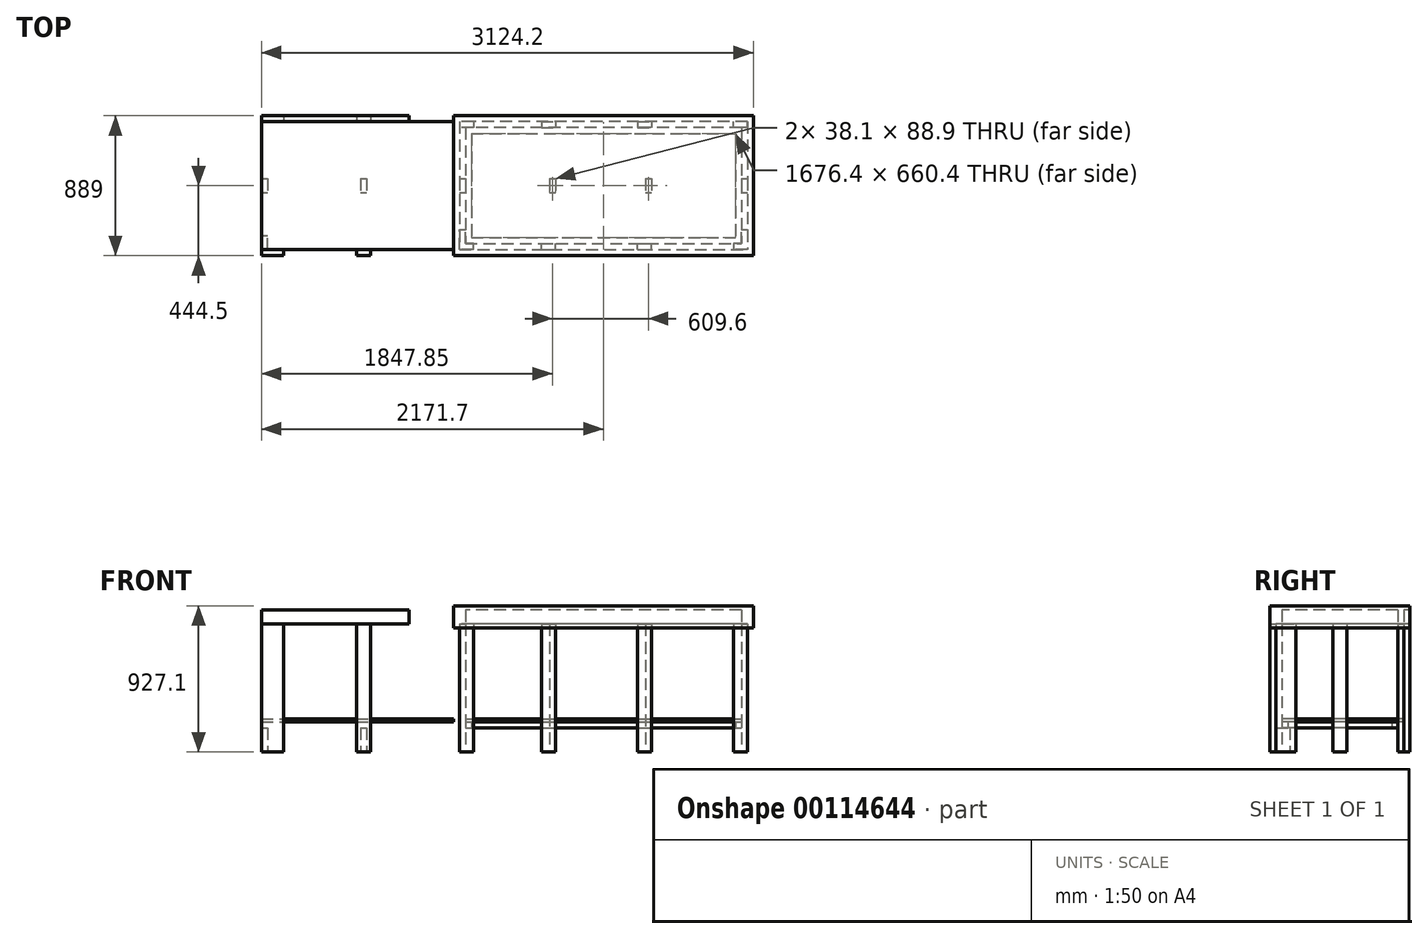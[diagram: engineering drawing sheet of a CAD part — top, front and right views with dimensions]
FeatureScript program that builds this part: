
annotation { "Feature Type Name" : "Feature", "Feature Type Description" : "" }
export const myFeature = defineFeature(function(context is Context, id is Id, definition is map)
    precondition{}
    {
        {
            var Q0;
            Q0=qCreatedBy(makeId("Top.planeOp"),FACE);
            cPlane(context, id + "F0", {"entities" : qUnion([Q0]), "cplaneType" : CPlaneType.OFFSET, "offset" : 152.4 * mm, "width" : 152.4 * mm, "height" : 152.4 * mm});
        }
        {
            var Q0;
            Q0=qCreatedBy(makeId("Top.planeOp"),FACE);
            var sketch = newSketch(context, id + "F1", { "sketchPlane" : qUnion([Q0])});
            skLineSegment(sketch, "E0.bottom", {"start": v(0, 0) * mm, "end": v(3124.2, 0) * mm});
            skLineSegment(sketch, "E0.top", {"start": v(0, 889) * mm, "end": v(3124.2, 889) * mm});
            skLineSegment(sketch, "E0.left", {"start": v(0, 0) * mm, "end": v(0, 889) * mm});
            skLineSegment(sketch, "E0.right", {"start": v(3124.2, 0) * mm, "end": v(3124.2, 889) * mm});
            skLineSegment(sketch, "E1.bottom", {"start": v(0, 889) * mm, "end": v(1295.4, 889) * mm});
            skLineSegment(sketch, "E1.top", {"start": v(0, 2184.4) * mm, "end": v(1295.4, 2184.4) * mm});
            skLineSegment(sketch, "E1.left", {"start": v(0, 889) * mm, "end": v(0, 2184.4) * mm});
            skLineSegment(sketch, "E1.right", {"start": v(1295.4, 889) * mm, "end": v(1295.4, 2184.4) * mm});
            skLineSegment(sketch, "E2.bottom", {"start": v(0, 0) * mm, "end": v(1295.4, 0) * mm});
            skLineSegment(sketch, "E2.top", {"start": v(0, -1295.4) * mm, "end": v(1295.4, -1295.4) * mm});
            skLineSegment(sketch, "E2.left", {"start": v(0, 0) * mm, "end": v(0, -1295.4) * mm});
            skLineSegment(sketch, "E2.right", {"start": v(1295.4, 0) * mm, "end": v(1295.4, -1295.4) * mm});
            skLineSegment(sketch, "E3.0", {"start": v(38.1, 927.1) * mm, "end": v(38.1, 2146.3) * mm});
            skLineSegment(sketch, "E3.1", {"start": v(38.1, 927.1) * mm, "end": v(1257.3, 927.1) * mm});
            skLineSegment(sketch, "E3.2", {"start": v(1257.3, 927.1) * mm, "end": v(1257.3, 2146.3) * mm});
            skLineSegment(sketch, "E3.3", {"start": v(38.1, 2146.3) * mm, "end": v(1257.3, 2146.3) * mm});
            skLineSegment(sketch, "E4.0", {"start": v(1257.3, -38.1) * mm, "end": v(1257.3, -1257.3) * mm});
            skLineSegment(sketch, "E4.1", {"start": v(38.1, -38.1) * mm, "end": v(1257.3, -38.1) * mm});
            skLineSegment(sketch, "E4.2", {"start": v(38.1, -38.1) * mm, "end": v(38.1, -1257.3) * mm});
            skLineSegment(sketch, "E4.3", {"start": v(38.1, -1257.3) * mm, "end": v(1257.3, -1257.3) * mm});
            skLineSegment(sketch, "E5.0", {"start": v(38.1, 38.1) * mm, "end": v(38.1, 850.9) * mm});
            skLineSegment(sketch, "E5.1", {"start": v(38.1, 38.1) * mm, "end": v(3086.1, 38.1) * mm});
            skLineSegment(sketch, "E5.2", {"start": v(3086.1, 38.1) * mm, "end": v(3086.1, 850.9) * mm});
            skLineSegment(sketch, "E5.3", {"start": v(38.1, 850.9) * mm, "end": v(3086.1, 850.9) * mm});
            skLineSegment(sketch, "E6", {"start": v(647.7, 2146.3) * mm, "end": v(647.7, 927.1) * mm, "construction": true});
            skLineSegment(sketch, "E7", {"start": v(38.1, 1536.7) * mm, "end": v(1257.3, 1536.7) * mm, "construction": true});
            skLineSegment(sketch, "E8", {"start": v(647.7, -38.1) * mm, "end": v(647.7, -1257.3) * mm, "construction": true});
            skLineSegment(sketch, "E9", {"start": v(38.1, -647.7) * mm, "end": v(1257.3, -647.7) * mm, "construction": true});
            skLineSegment(sketch, "E10", {"start": v(38.1, 444.5) * mm, "end": v(3086.1, 444.5) * mm, "construction": true});
            skSolve(sketch);
        }
        {
            var Q0;
            Q0=qCreatedBy(makeId("Top.planeOp"),FACE);
            var sketch = newSketch(context, id + "F2", { "sketchPlane" : qUnion([Q0])});
            skLineSegment(sketch, "E11.bottom", {"start": v(3086.1, 812.8) * mm, "end": v(2997.2, 812.8) * mm});
            skLineSegment(sketch, "E11.top", {"start": v(3086.1, 850.9) * mm, "end": v(2997.2, 850.9) * mm});
            skLineSegment(sketch, "E11.left", {"start": v(3086.1, 812.8) * mm, "end": v(3086.1, 850.9) * mm});
            skLineSegment(sketch, "E11.right", {"start": v(2997.2, 812.8) * mm, "end": v(2997.2, 850.9) * mm});
            skLineSegment(sketch, "E12.bottom", {"start": v(3048, 812.8) * mm, "end": v(3086.1, 812.8) * mm});
            skLineSegment(sketch, "E12.top", {"start": v(3048, 723.9) * mm, "end": v(3086.1, 723.9) * mm});
            skLineSegment(sketch, "E12.left", {"start": v(3048, 812.8) * mm, "end": v(3048, 723.9) * mm});
            skLineSegment(sketch, "E12.right", {"start": v(3086.1, 812.8) * mm, "end": v(3086.1, 723.9) * mm});
            skLineSegment(sketch, "E13.bottom", {"start": v(2387.6, 850.9) * mm, "end": v(2476.5, 850.9) * mm});
            skLineSegment(sketch, "E13.top", {"start": v(2387.6, 812.8) * mm, "end": v(2476.5, 812.8) * mm});
            skLineSegment(sketch, "E13.left", {"start": v(2387.6, 850.9) * mm, "end": v(2387.6, 812.8) * mm});
            skLineSegment(sketch, "E13.right", {"start": v(2476.5, 850.9) * mm, "end": v(2476.5, 812.8) * mm});
            skLineSegment(sketch, "E14.bottom", {"start": v(1778, 850.9) * mm, "end": v(1866.9, 850.9) * mm});
            skLineSegment(sketch, "E14.top", {"start": v(1778, 812.8) * mm, "end": v(1866.9, 812.8) * mm});
            skLineSegment(sketch, "E14.left", {"start": v(1778, 850.9) * mm, "end": v(1778, 812.8) * mm});
            skLineSegment(sketch, "E14.right", {"start": v(1866.9, 850.9) * mm, "end": v(1866.9, 812.8) * mm});
            skLineSegment(sketch, "E15.bottom", {"start": v(1346.2, 850.9) * mm, "end": v(1257.3, 850.9) * mm});
            skLineSegment(sketch, "E15.top", {"start": v(1346.2, 812.8) * mm, "end": v(1257.3, 812.8) * mm});
            skLineSegment(sketch, "E15.left", {"start": v(1346.2, 850.9) * mm, "end": v(1346.2, 812.8) * mm});
            skLineSegment(sketch, "E15.right", {"start": v(1257.3, 850.9) * mm, "end": v(1257.3, 812.8) * mm});
            skLineSegment(sketch, "E16.bottom", {"start": v(1257.3, 812.8) * mm, "end": v(1295.4, 812.8) * mm});
            skLineSegment(sketch, "E16.top", {"start": v(1257.3, 723.9) * mm, "end": v(1295.4, 723.9) * mm});
            skLineSegment(sketch, "E16.left", {"start": v(1257.3, 812.8) * mm, "end": v(1257.3, 723.9) * mm});
            skLineSegment(sketch, "E16.right", {"start": v(1295.4, 812.8) * mm, "end": v(1295.4, 723.9) * mm});
            skPoint(sketch, "E17", {"position": v(1301.75, 812.8) * mm});
            skLineSegment(sketch, "E18.bottom", {"start": v(0, 889) * mm, "end": v(139.7, 889) * mm});
            skLineSegment(sketch, "E18.top", {"start": v(0, 850.9) * mm, "end": v(139.7, 850.9) * mm});
            skLineSegment(sketch, "E18.left", {"start": v(0, 889) * mm, "end": v(0, 850.9) * mm});
            skLineSegment(sketch, "E18.right", {"start": v(139.7, 889) * mm, "end": v(139.7, 850.9) * mm});
            skLineSegment(sketch, "E19.bottom", {"start": v(0, 850.9) * mm, "end": v(38.1, 850.9) * mm});
            skLineSegment(sketch, "E19.top", {"start": v(0, 762) * mm, "end": v(38.1, 762) * mm});
            skLineSegment(sketch, "E19.left", {"start": v(0, 850.9) * mm, "end": v(0, 762) * mm});
            skLineSegment(sketch, "E19.right", {"start": v(38.1, 850.9) * mm, "end": v(38.1, 762) * mm});
            skLineSegment(sketch, "E20.bottom", {"start": v(603.25, 889) * mm, "end": v(692.15, 889) * mm});
            skLineSegment(sketch, "E20.top", {"start": v(603.25, 850.9) * mm, "end": v(692.15, 850.9) * mm});
            skLineSegment(sketch, "E20.left", {"start": v(603.25, 889) * mm, "end": v(603.25, 850.9) * mm});
            skLineSegment(sketch, "E20.right", {"start": v(692.15, 889) * mm, "end": v(692.15, 850.9) * mm});
            skPoint(sketch, "E21", {"position": v(647.7, 850.9) * mm});
            skLineSegment(sketch, "E22.MirrorCS", {"start": v(0, 38.1) * mm, "end": v(38.1, 38.1) * mm});
            skLineSegment(sketch, "E23.MirrorCS", {"start": v(0, 0) * mm, "end": v(0, 38.1) * mm});
            skLineSegment(sketch, "E24.MirrorCS", {"start": v(3086.1, 76.2) * mm, "end": v(3086.1, 38.1) * mm});
            skLineSegment(sketch, "E25.MirrorCS", {"start": v(3048, 76.2) * mm, "end": v(3086.1, 76.2) * mm});
            skLineSegment(sketch, "E26.MirrorCS", {"start": v(1257.3, 76.2) * mm, "end": v(1295.4, 76.2) * mm});
            skLineSegment(sketch, "E27.MirrorCS", {"start": v(3048, 165.1) * mm, "end": v(3086.1, 165.1) * mm});
            skLineSegment(sketch, "E28.MirrorCS", {"start": v(0, 127) * mm, "end": v(38.1, 127) * mm});
            skLineSegment(sketch, "E29.MirrorCS", {"start": v(1778, 76.2) * mm, "end": v(1866.9, 76.2) * mm});
            skLineSegment(sketch, "E30.MirrorCS", {"start": v(38.1, 38.1) * mm, "end": v(38.1, 127) * mm});
            skLineSegment(sketch, "E31.MirrorCS", {"start": v(1778, 38.1) * mm, "end": v(1778, 76.2) * mm});
            skLineSegment(sketch, "E32.MirrorCS", {"start": v(3086.1, 76.2) * mm, "end": v(2997.2, 76.2) * mm});
            skLineSegment(sketch, "E33.MirrorCS", {"start": v(1778, 38.1) * mm, "end": v(1866.9, 38.1) * mm});
            skLineSegment(sketch, "E34.MirrorCS", {"start": v(1257.3, 76.2) * mm, "end": v(1257.3, 165.1) * mm});
            skLineSegment(sketch, "E35.MirrorCS", {"start": v(2997.2, 76.2) * mm, "end": v(2997.2, 38.1) * mm});
            skLineSegment(sketch, "E36.MirrorCS", {"start": v(1295.4, 76.2) * mm, "end": v(1295.4, 165.1) * mm});
            skLineSegment(sketch, "E37.MirrorCS", {"start": v(139.7, 0) * mm, "end": v(139.7, 38.1) * mm});
            skLineSegment(sketch, "E38.MirrorCS", {"start": v(3048, 76.2) * mm, "end": v(3048, 165.1) * mm});
            skLineSegment(sketch, "E39.MirrorCS", {"start": v(1346.2, 38.1) * mm, "end": v(1346.2, 76.2) * mm});
            skLineSegment(sketch, "E40.MirrorCS", {"start": v(3086.1, 76.2) * mm, "end": v(3086.1, 165.1) * mm});
            skLineSegment(sketch, "E41.MirrorCS", {"start": v(692.15, 0) * mm, "end": v(692.15, 38.1) * mm});
            skLineSegment(sketch, "E42.MirrorCS", {"start": v(0, 38.1) * mm, "end": v(0, 127) * mm});
            skLineSegment(sketch, "E43.MirrorCS", {"start": v(1257.3, 38.1) * mm, "end": v(1257.3, 76.2) * mm});
            skLineSegment(sketch, "E44.MirrorCS", {"start": v(603.25, 0) * mm, "end": v(692.15, 0) * mm});
            skLineSegment(sketch, "E45.MirrorCS", {"start": v(1346.2, 76.2) * mm, "end": v(1257.3, 76.2) * mm});
            skLineSegment(sketch, "E46.MirrorCS", {"start": v(603.25, 38.1) * mm, "end": v(692.15, 38.1) * mm});
            skLineSegment(sketch, "E47.MirrorCS", {"start": v(2476.5, 38.1) * mm, "end": v(2476.5, 76.2) * mm});
            skLineSegment(sketch, "E48.MirrorCS", {"start": v(603.25, 0) * mm, "end": v(603.25, 38.1) * mm});
            skLineSegment(sketch, "E49.MirrorCS", {"start": v(2387.6, 38.1) * mm, "end": v(2387.6, 76.2) * mm});
            skLineSegment(sketch, "E50.MirrorCS", {"start": v(2387.6, 76.2) * mm, "end": v(2476.5, 76.2) * mm});
            skLineSegment(sketch, "E51.MirrorCS", {"start": v(1257.3, 165.1) * mm, "end": v(1295.4, 165.1) * mm});
            skLineSegment(sketch, "E52.MirrorCS", {"start": v(1866.9, 38.1) * mm, "end": v(1866.9, 76.2) * mm});
            skLineSegment(sketch, "E53.MirrorCS", {"start": v(2387.6, 38.1) * mm, "end": v(2476.5, 38.1) * mm});
            skLineSegment(sketch, "E54.MirrorCS", {"start": v(1346.2, 38.1) * mm, "end": v(1257.3, 38.1) * mm});
            skLineSegment(sketch, "E55.MirrorCS", {"start": v(0, 38.1) * mm, "end": v(139.7, 38.1) * mm});
            skLineSegment(sketch, "E56.MirrorCS", {"start": v(0, 0) * mm, "end": v(139.7, 0) * mm});
            skLineSegment(sketch, "E57.MirrorCS", {"start": v(3086.1, 38.1) * mm, "end": v(2997.2, 38.1) * mm});
            skPoint(sketch, "E58.MirrorP", {"position": v(1301.75, 76.2) * mm});
            skPoint(sketch, "E59.MirrorP", {"position": v(647.7, 38.1) * mm});
            skLineSegment(sketch, "E60.bottom", {"start": v(2438.4, 488.95) * mm, "end": v(2476.5, 488.95) * mm});
            skLineSegment(sketch, "E60.top", {"start": v(2438.4, 400.05) * mm, "end": v(2476.5, 400.05) * mm});
            skLineSegment(sketch, "E60.left", {"start": v(2438.4, 488.95) * mm, "end": v(2438.4, 400.05) * mm});
            skLineSegment(sketch, "E60.right", {"start": v(2476.5, 488.95) * mm, "end": v(2476.5, 400.05) * mm});
            skPoint(sketch, "E61", {"position": v(2438.4, 444.5) * mm});
            skLineSegment(sketch, "E62.bottom", {"start": v(3048, 488.95) * mm, "end": v(3086.1, 488.95) * mm});
            skLineSegment(sketch, "E62.top", {"start": v(3048, 400.05) * mm, "end": v(3086.1, 400.05) * mm});
            skLineSegment(sketch, "E62.left", {"start": v(3048, 488.95) * mm, "end": v(3048, 400.05) * mm});
            skLineSegment(sketch, "E62.right", {"start": v(3086.1, 488.95) * mm, "end": v(3086.1, 400.05) * mm});
            skPoint(sketch, "E63", {"position": v(3086.1, 444.5) * mm});
            skLineSegment(sketch, "E64.bottom", {"start": v(1828.8, 488.95) * mm, "end": v(1866.9, 488.95) * mm});
            skLineSegment(sketch, "E64.top", {"start": v(1828.8, 400.05) * mm, "end": v(1866.9, 400.05) * mm});
            skLineSegment(sketch, "E64.left", {"start": v(1828.8, 488.95) * mm, "end": v(1828.8, 400.05) * mm});
            skLineSegment(sketch, "E64.right", {"start": v(1866.9, 488.95) * mm, "end": v(1866.9, 400.05) * mm});
            skPoint(sketch, "E65", {"position": v(1828.8, 444.5) * mm});
            skLineSegment(sketch, "E66.bottom", {"start": v(1257.3, 488.95) * mm, "end": v(1295.4, 488.95) * mm});
            skLineSegment(sketch, "E66.top", {"start": v(1257.3, 400.05) * mm, "end": v(1295.4, 400.05) * mm});
            skLineSegment(sketch, "E66.left", {"start": v(1257.3, 488.95) * mm, "end": v(1257.3, 400.05) * mm});
            skLineSegment(sketch, "E66.right", {"start": v(1295.4, 488.95) * mm, "end": v(1295.4, 400.05) * mm});
            skPoint(sketch, "E67", {"position": v(1295.4, 444.5) * mm});
            skLineSegment(sketch, "E68.bottom", {"start": v(628.65, 488.95) * mm, "end": v(666.75, 488.95) * mm});
            skLineSegment(sketch, "E68.top", {"start": v(628.65, 400.05) * mm, "end": v(666.75, 400.05) * mm});
            skLineSegment(sketch, "E68.left", {"start": v(628.65, 488.95) * mm, "end": v(628.65, 400.05) * mm});
            skLineSegment(sketch, "E68.right", {"start": v(666.75, 488.95) * mm, "end": v(666.75, 400.05) * mm});
            skLineSegment(sketch, "E69.bottom", {"start": v(0, 488.95) * mm, "end": v(38.1, 488.95) * mm});
            skLineSegment(sketch, "E69.top", {"start": v(0, 400.05) * mm, "end": v(38.1, 400.05) * mm});
            skLineSegment(sketch, "E69.left", {"start": v(0, 488.95) * mm, "end": v(0, 400.05) * mm});
            skLineSegment(sketch, "E69.right", {"start": v(38.1, 488.95) * mm, "end": v(38.1, 400.05) * mm});
            skPoint(sketch, "E70", {"position": v(0, 444.5) * mm});
            skPoint(sketch, "E71", {"position": v(647.7, 488.95) * mm});
            skPoint(sketch, "E72", {"position": v(628.65, 444.5) * mm});
            skSolve(sketch);
        }
        {
            var Q0;
            Q0=makeQuery(id+"F2.imprint","IMPRINT",FACE,{"disambiguationData":[TD([[makeQuery(id+"F2.imprint","IMPRINT",EDGE,{"derivedFrom":sQuery(id+"F2.wireOp",EDGE,"E13.bottom")}),-1.0]])]});
            var Q1;
            Q1=makeQuery(id+"F2.imprint","IMPRINT",FACE,{"disambiguationData":[TD([[makeQuery(id+"F2.imprint","IMPRINT",EDGE,{"derivedFrom":sQuery(id+"F2.wireOp",EDGE,"E14.bottom")}),-1.0]])]});
            var Q2;
            Q2=makeQuery(id+"F2.imprint","IMPRINT",FACE,{"disambiguationData":[TD([[makeQuery(id+"F2.imprint","IMPRINT",EDGE,{"derivedFrom":sQuery(id+"F2.wireOp",EDGE,"E20.bottom")}),-1.0]])]});
            var Q3;
            Q3=makeQuery(id+"F2.imprint","IMPRINT",FACE,{"disambiguationData":[TD([[makeQuery(id+"F2.imprint","IMPRINT",EDGE,{"derivedFrom":sQuery(id+"F2.wireOp",EDGE,"E29.MirrorCS")}),-1.0]])]});
            var Q4;
            Q4=makeQuery(id+"F2.imprint","IMPRINT",FACE,{"disambiguationData":[TD([[makeQuery(id+"F2.imprint","IMPRINT",EDGE,{"derivedFrom":sQuery(id+"F2.wireOp",EDGE,"E41.MirrorCS")}),1.0]])]});
            var Q5;
            Q5=makeQuery(id+"F2.imprint","IMPRINT",FACE,{"disambiguationData":[TD([[makeQuery(id+"F2.imprint","IMPRINT",EDGE,{"derivedFrom":sQuery(id+"F2.wireOp",EDGE,"E47.MirrorCS")}),1.0]])]});
            var Q6;
            Q6=makeQuery(id+"F2.imprint","IMPRINT",FACE,{"disambiguationData":[TD([[makeQuery(id+"F2.imprint","IMPRINT",EDGE,{"derivedFrom":sQuery(id+"F2.wireOp",EDGE,"E60.bottom")}),-1.0]])]});
            var Q7;
            Q7=makeQuery(id+"F2.imprint","IMPRINT",FACE,{"disambiguationData":[TD([[makeQuery(id+"F2.imprint","IMPRINT",EDGE,{"derivedFrom":sQuery(id+"F2.wireOp",EDGE,"E62.bottom")}),-1.0]])]});
            var Q8;
            Q8=makeQuery(id+"F2.imprint","IMPRINT",FACE,{"disambiguationData":[TD([[makeQuery(id+"F2.imprint","IMPRINT",EDGE,{"derivedFrom":sQuery(id+"F2.wireOp",EDGE,"E64.bottom")}),-1.0]])]});
            var Q9;
            Q9=makeQuery(id+"F2.imprint","IMPRINT",FACE,{"disambiguationData":[TD([[makeQuery(id+"F2.imprint","IMPRINT",EDGE,{"derivedFrom":sQuery(id+"F2.wireOp",EDGE,"E66.bottom")}),-1.0]])]});
            var Q10;
            Q10=makeQuery(id+"F2.imprint","IMPRINT",FACE,{"disambiguationData":[TD([[makeQuery(id+"F2.imprint","IMPRINT",EDGE,{"derivedFrom":sQuery(id+"F2.wireOp",EDGE,"E11.bottom")}),-1.0]])]});
            var Q11;
            Q11=makeQuery(id+"F2.imprint","IMPRINT",FACE,{"disambiguationData":[TD([[makeQuery(id+"F2.imprint","IMPRINT",EDGE,{"derivedFrom":sQuery(id+"F2.wireOp",EDGE,"E12.bottom")}),-1.0]])]});
            var Q12;
            Q12=makeQuery(id+"F2.imprint","IMPRINT",FACE,{"disambiguationData":[TD([[makeQuery(id+"F2.imprint","IMPRINT",EDGE,{"derivedFrom":sQuery(id+"F2.wireOp",EDGE,"E15.bottom")}),1.0]])]});
            var Q13;
            Q13=makeQuery(id+"F2.imprint","IMPRINT",FACE,{"disambiguationData":[TD([[makeQuery(id+"F2.imprint","IMPRINT",EDGE,{"derivedFrom":sQuery(id+"F2.wireOp",EDGE,"E16.bottom")}),-1.0]])]});
            var Q14;
            Q14=makeQuery(id+"F2.imprint","IMPRINT",FACE,{"disambiguationData":[TD([[makeQuery(id+"F2.imprint","IMPRINT",EDGE,{"derivedFrom":sQuery(id+"F2.wireOp",EDGE,"E18.bottom")}),-1.0]])]});
            var Q15;
            {var subQ3=sQuery(id+"F2.wireOp",EDGE,"E23.MirrorCS");Q15=makeQuery(id+"F2.imprint","IMPRINT",FACE,{"disambiguationData":[TD([[makeQuery(id+"F2.imprint","IMPRINT",EDGE,{"derivedFrom":subQ3}),-1.0]])]});}
            var Q16;
            {var subQ3=sQuery(id+"F2.wireOp",EDGE,"E24.MirrorCS");Q16=makeQuery(id+"F2.imprint","IMPRINT",FACE,{"disambiguationData":[TD([[makeQuery(id+"F2.imprint","IMPRINT",EDGE,{"derivedFrom":subQ3}),-1.0]])]});}
            var Q17;
            Q17=makeQuery(id+"F2.imprint","IMPRINT",FACE,{"disambiguationData":[TD([[makeQuery(id+"F2.imprint","IMPRINT",EDGE,{"derivedFrom":sQuery(id+"F2.wireOp",EDGE,"E27.MirrorCS")}),-1.0]])]});
            var Q18;
            {var subQ0=sQuery(id+"F2.wireOp",EDGE,"E34.MirrorCS");Q18=makeQuery(id+"F2.imprint","IMPRINT",FACE,{"disambiguationData":[TD([[makeQuery(id+"F2.imprint","IMPRINT",EDGE,{"derivedFrom":subQ0}),-1.0]])]});}
            var Q19;
            {var subQ4=sQuery(id+"F2.wireOp",EDGE,"E39.MirrorCS");Q19=makeQuery(id+"F2.imprint","IMPRINT",FACE,{"disambiguationData":[TD([[makeQuery(id+"F2.imprint","IMPRINT",EDGE,{"derivedFrom":subQ4}),1.0]])]});}
            extrude(context, id + "F3", {"entities" : qUnion([Q0, Q1, Q2, Q3, Q4, Q5, Q6, Q7, Q8, Q9, Q10, Q11, Q12, Q13, Q14, Q15, Q16, Q17, Q18, Q19]), "depth" : 812.8 * mm});
        }
        {
            var Q0;
            Q0=makeQuery(id+"F2.imprint","IMPRINT",FACE,{"disambiguationData":[TD([[makeQuery(id+"F2.imprint","IMPRINT",EDGE,{"derivedFrom":sQuery(id+"F2.wireOp",EDGE,"E69.bottom")}),-1.0]])]});
            var Q1;
            Q1=makeQuery(id+"F2.imprint","IMPRINT",FACE,{"disambiguationData":[TD([[makeQuery(id+"F2.imprint","IMPRINT",EDGE,{"derivedFrom":sQuery(id+"F2.wireOp",EDGE,"E68.bottom")}),-1.0]])]});
            var Q2;
            Q2=makeQuery(id+"F2.imprint","IMPRINT",FACE,{"disambiguationData":[TD([[makeQuery(id+"F2.imprint","IMPRINT",EDGE,{"derivedFrom":sQuery(id+"F2.wireOp",EDGE,"E19.bottom")}),-1.0]])]});
            var Q3;
            Q3=makeQuery(id+"F2.imprint","IMPRINT",FACE,{"disambiguationData":[TD([[makeQuery(id+"F2.imprint","IMPRINT",EDGE,{"derivedFrom":sQuery(id+"F2.wireOp",EDGE,"E28.MirrorCS")}),-1.0]])]});
            extrude(context, id + "F4", {"entities" : qUnion([Q0, Q1, Q2, Q3]), "depth" : 152.4 * mm});
        }
        {
            var Q0;
            Q0=qCreatedBy(id+"F0.planeOp",FACE);
            var sketch = newSketch(context, id + "F5", { "sketchPlane" : qUnion([Q0])});
            skLineSegment(sketch, "E73.bottom", {"start": v(1295.4, 812.8) * mm, "end": v(3048, 812.8) * mm});
            skLineSegment(sketch, "E73.top", {"start": v(1295.4, 774.7) * mm, "end": v(3048, 774.7) * mm});
            skLineSegment(sketch, "E73.left", {"start": v(1295.4, 812.8) * mm, "end": v(1295.4, 774.7) * mm});
            skLineSegment(sketch, "E73.right", {"start": v(3048, 812.8) * mm, "end": v(3048, 774.7) * mm});
            skLineSegment(sketch, "E74.MirrorCS", {"start": v(1295.4, 76.2) * mm, "end": v(1295.4, 114.3) * mm});
            skLineSegment(sketch, "E75.MirrorCS", {"start": v(3048, 76.2) * mm, "end": v(3048, 114.3) * mm});
            skLineSegment(sketch, "E76.MirrorCS", {"start": v(1295.4, 114.3) * mm, "end": v(3048, 114.3) * mm});
            skLineSegment(sketch, "E77.MirrorCS", {"start": v(1295.4, 76.2) * mm, "end": v(3048, 76.2) * mm});
            skLineSegment(sketch, "E78.bottom", {"start": v(3048, 774.7) * mm, "end": v(3009.9, 774.7) * mm});
            skLineSegment(sketch, "E78.top", {"start": v(3048, 114.3) * mm, "end": v(3009.9, 114.3) * mm});
            skLineSegment(sketch, "E78.left", {"start": v(3048, 774.7) * mm, "end": v(3048, 114.3) * mm});
            skLineSegment(sketch, "E78.right", {"start": v(3009.9, 774.7) * mm, "end": v(3009.9, 114.3) * mm});
            skLineSegment(sketch, "E79.bottom", {"start": v(2400.3, 774.7) * mm, "end": v(2438.4, 774.7) * mm});
            skLineSegment(sketch, "E79.top", {"start": v(2400.3, 114.3) * mm, "end": v(2438.4, 114.3) * mm});
            skLineSegment(sketch, "E79.left", {"start": v(2400.3, 774.7) * mm, "end": v(2400.3, 114.3) * mm});
            skLineSegment(sketch, "E79.right", {"start": v(2438.4, 774.7) * mm, "end": v(2438.4, 114.3) * mm});
            skLineSegment(sketch, "E80.bottom", {"start": v(1790.7, 774.7) * mm, "end": v(1828.8, 774.7) * mm});
            skLineSegment(sketch, "E80.top", {"start": v(1790.7, 114.3) * mm, "end": v(1828.8, 114.3) * mm});
            skLineSegment(sketch, "E80.left", {"start": v(1790.7, 774.7) * mm, "end": v(1790.7, 114.3) * mm});
            skLineSegment(sketch, "E80.right", {"start": v(1828.8, 774.7) * mm, "end": v(1828.8, 114.3) * mm});
            skLineSegment(sketch, "E81.bottom", {"start": v(1295.4, 774.7) * mm, "end": v(1333.5, 774.7) * mm});
            skLineSegment(sketch, "E81.top", {"start": v(1295.4, 114.3) * mm, "end": v(1333.5, 114.3) * mm});
            skLineSegment(sketch, "E81.left", {"start": v(1295.4, 774.7) * mm, "end": v(1295.4, 114.3) * mm});
            skLineSegment(sketch, "E81.right", {"start": v(1333.5, 774.7) * mm, "end": v(1333.5, 114.3) * mm});
            skSolve(sketch);
        }
        {
            var Q0;
            Q0 = qSketchRegion(id + "F5", true);
            var Q1;
            Q1=makeQuery(id+"F5.imprint","IMPRINT",FACE,{"disambiguationData":[TD([[makeQuery(id+"F5.imprint","IMPRINT",EDGE,{"derivedFrom":sQuery(id+"F5.wireOp",EDGE,"E80.bottom")}),-1.0]])]});
            var Q2;
            Q2=makeQuery(id+"F5.imprint","IMPRINT",FACE,{"disambiguationData":[TD([[makeQuery(id+"F5.imprint","IMPRINT",EDGE,{"derivedFrom":sQuery(id+"F5.wireOp",EDGE,"E79.bottom")}),-1.0]])]});
            var Q3;
            Q3=makeQuery(id+"F5.imprint","IMPRINT",FACE,{"disambiguationData":[TD([[makeQuery(id+"F5.imprint","IMPRINT",EDGE,{"derivedFrom":sQuery(id+"F5.wireOp",EDGE,"S6wTpKe9-ayNI-EvME-aKKF-vAW1G7L7wr7T.bottom")}),-1.0]])]});
            extrude(context, id + "F6", {"entities" : qUnion([Q0, Q1, Q2, Q3]), "depth" : 38.1 * mm});
        }
        {
            var Q0;
            Q0=makeQuery(id+"F6.opExtrude","CAP_FACE",FACE,{"disambiguationData":[OSD([sQuery(id+"F5.wireOp",EDGE,"E73.bottom"),sQuery(id+"F5.wireOp",EDGE,"E73.top"),sQuery(id+"F5.wireOp",EDGE,"E73.left"),sQuery(id+"F5.wireOp",EDGE,"E73.right"),sQuery(id+"F5.wireOp",EDGE,"E74.MirrorCS"),sQuery(id+"F5.wireOp",EDGE,"E75.MirrorCS"),sQuery(id+"F5.wireOp",EDGE,"E76.MirrorCS"),sQuery(id+"F5.wireOp",EDGE,"E77.MirrorCS"),sQuery(id+"F5.wireOp",EDGE,"E78.left"),sQuery(id+"F5.wireOp",EDGE,"E78.right"),sQuery(id+"F5.wireOp",EDGE,"E79.left"),sQuery(id+"F5.wireOp",EDGE,"E79.right"),sQuery(id+"F5.wireOp",EDGE,"E80.left"),sQuery(id+"F5.wireOp",EDGE,"E80.right"),sQuery(id+"F5.wireOp",EDGE,"E81.left"),sQuery(id+"F5.wireOp",EDGE,"E81.right")])],"isStart":false});
            var sketch = newSketch(context, id + "F7", { "sketchPlane" : qUnion([Q0])});
            skLineSegment(sketch, "E82.bottom", {"start": v(1295.4, 812.8) * mm, "end": v(3048, 812.8) * mm});
            skLineSegment(sketch, "E82.top", {"start": v(1295.4, 76.2) * mm, "end": v(3048, 76.2) * mm});
            skLineSegment(sketch, "E82.left", {"start": v(1295.4, 812.8) * mm, "end": v(1295.4, 76.2) * mm});
            skLineSegment(sketch, "E82.right", {"start": v(3048, 812.8) * mm, "end": v(3048, 76.2) * mm});
            skLineSegment(sketch, "E83.bottom", {"start": v(1828.8, 488.95) * mm, "end": v(1866.9, 488.95) * mm});
            skLineSegment(sketch, "E83.top", {"start": v(1828.8, 400.05) * mm, "end": v(1866.9, 400.05) * mm});
            skLineSegment(sketch, "E83.left", {"start": v(1828.8, 488.95) * mm, "end": v(1828.8, 400.05) * mm});
            skLineSegment(sketch, "E83.right", {"start": v(1866.9, 488.95) * mm, "end": v(1866.9, 400.05) * mm});
            skLineSegment(sketch, "E84.bottom", {"start": v(2438.4, 488.95) * mm, "end": v(2476.5, 488.95) * mm});
            skLineSegment(sketch, "E84.top", {"start": v(2438.4, 400.05) * mm, "end": v(2476.5, 400.05) * mm});
            skLineSegment(sketch, "E84.left", {"start": v(2438.4, 488.95) * mm, "end": v(2438.4, 400.05) * mm});
            skLineSegment(sketch, "E84.right", {"start": v(2476.5, 488.95) * mm, "end": v(2476.5, 400.05) * mm});
            skLineSegment(sketch, "E85.bottom", {"start": v(0, 850.9) * mm, "end": v(1219.2, 850.9) * mm});
            skLineSegment(sketch, "E85.top", {"start": v(0, 38.1) * mm, "end": v(1219.2, 38.1) * mm});
            skLineSegment(sketch, "E85.left", {"start": v(0, 850.9) * mm, "end": v(0, 38.1) * mm});
            skLineSegment(sketch, "E85.right", {"start": v(1219.2, 850.9) * mm, "end": v(1219.2, 38.1) * mm});
            skSolve(sketch);
        }
        {
            var Q0;
            Q0 = qSketchRegion(id + "F7", true);
            extrude(context, id + "F8", {"entities" : qUnion([Q0]), "depth" : 19.05 * mm});
        }
        {
            var Q0;
            Q0=makeQuery(id+"F3.opExtrude","CAP_FACE",FACE,{"disambiguationData":[OSD([sQuery(id+"F2.wireOp",EDGE,"E15.bottom"),sQuery(id+"F2.wireOp",EDGE,"E15.top"),sQuery(id+"F2.wireOp",EDGE,"E15.left"),sQuery(id+"F2.wireOp",EDGE,"E15.right"),sQuery(id+"F2.wireOp",EDGE,"E16.top"),sQuery(id+"F2.wireOp",EDGE,"E16.left"),sQuery(id+"F2.wireOp",EDGE,"E16.right")])],"isStart":false});
            var sketch = newSketch(context, id + "F9", { "sketchPlane" : qUnion([Q0])});
            skLineSegment(sketch, "E86.bottom", {"start": v(1295.4, 850.9) * mm, "end": v(3048, 850.9) * mm});
            skLineSegment(sketch, "E86.top", {"start": v(1295.4, 812.8) * mm, "end": v(3048, 812.8) * mm});
            skLineSegment(sketch, "E86.left", {"start": v(1295.4, 850.9) * mm, "end": v(1295.4, 812.8) * mm});
            skLineSegment(sketch, "E86.right", {"start": v(3048, 850.9) * mm, "end": v(3048, 812.8) * mm});
            skLineSegment(sketch, "E87.bottom", {"start": v(3048, 850.9) * mm, "end": v(3086.1, 850.9) * mm});
            skLineSegment(sketch, "E87.top", {"start": v(3048, 38.1) * mm, "end": v(3086.1, 38.1) * mm});
            skLineSegment(sketch, "E87.left", {"start": v(3048, 850.9) * mm, "end": v(3048, 38.1) * mm});
            skLineSegment(sketch, "E87.right", {"start": v(3086.1, 850.9) * mm, "end": v(3086.1, 38.1) * mm});
            skLineSegment(sketch, "E88.bottom", {"start": v(1257.3, 850.9) * mm, "end": v(1295.4, 850.9) * mm});
            skLineSegment(sketch, "E88.top", {"start": v(1257.3, 38.1) * mm, "end": v(1295.4, 38.1) * mm});
            skLineSegment(sketch, "E88.left", {"start": v(1257.3, 850.9) * mm, "end": v(1257.3, 38.1) * mm});
            skLineSegment(sketch, "E88.right", {"start": v(1295.4, 850.9) * mm, "end": v(1295.4, 38.1) * mm});
            skLineSegment(sketch, "E89.MirrorCS", {"start": v(1295.4, 38.1) * mm, "end": v(1295.4, 76.2) * mm});
            skLineSegment(sketch, "E90.MirrorCS", {"start": v(3048, 38.1) * mm, "end": v(3048, 76.2) * mm});
            skLineSegment(sketch, "E91.MirrorCS", {"start": v(1295.4, 76.2) * mm, "end": v(3048, 76.2) * mm});
            skLineSegment(sketch, "E92.MirrorCS", {"start": v(1295.4, 38.1) * mm, "end": v(3048, 38.1) * mm});
            skLineSegment(sketch, "E93.bottom", {"start": v(1866.9, 812.8) * mm, "end": v(1828.8, 812.8) * mm});
            skLineSegment(sketch, "E93.top", {"start": v(1866.9, 76.2) * mm, "end": v(1828.8, 76.2) * mm});
            skLineSegment(sketch, "E93.left", {"start": v(1866.9, 812.8) * mm, "end": v(1866.9, 76.2) * mm});
            skLineSegment(sketch, "E93.right", {"start": v(1828.8, 812.8) * mm, "end": v(1828.8, 76.2) * mm});
            skLineSegment(sketch, "E94.bottom", {"start": v(2476.5, 812.8) * mm, "end": v(2438.4, 812.8) * mm});
            skLineSegment(sketch, "E94.top", {"start": v(2476.5, 76.2) * mm, "end": v(2438.4, 76.2) * mm});
            skLineSegment(sketch, "E94.left", {"start": v(2476.5, 812.8) * mm, "end": v(2476.5, 76.2) * mm});
            skLineSegment(sketch, "E94.right", {"start": v(2438.4, 812.8) * mm, "end": v(2438.4, 76.2) * mm});
            skLineSegment(sketch, "E95.bottom", {"start": v(2781.3, 812.8) * mm, "end": v(2743.2, 812.8) * mm});
            skLineSegment(sketch, "E95.top", {"start": v(2781.3, 76.2) * mm, "end": v(2743.2, 76.2) * mm});
            skLineSegment(sketch, "E95.left", {"start": v(2781.3, 812.8) * mm, "end": v(2781.3, 76.2) * mm});
            skLineSegment(sketch, "E95.right", {"start": v(2743.2, 812.8) * mm, "end": v(2743.2, 76.2) * mm});
            skLineSegment(sketch, "E96.bottom", {"start": v(2171.7, 812.8) * mm, "end": v(2133.6, 812.8) * mm});
            skLineSegment(sketch, "E96.top", {"start": v(2171.7, 76.2) * mm, "end": v(2133.6, 76.2) * mm});
            skLineSegment(sketch, "E96.left", {"start": v(2171.7, 812.8) * mm, "end": v(2171.7, 76.2) * mm});
            skLineSegment(sketch, "E96.right", {"start": v(2133.6, 812.8) * mm, "end": v(2133.6, 76.2) * mm});
            skLineSegment(sketch, "E97.bottom", {"start": v(1581.15, 812.8) * mm, "end": v(1543.05, 812.8) * mm});
            skLineSegment(sketch, "E97.top", {"start": v(1581.15, 76.2) * mm, "end": v(1543.05, 76.2) * mm});
            skLineSegment(sketch, "E97.left", {"start": v(1581.15, 812.8) * mm, "end": v(1581.15, 76.2) * mm});
            skLineSegment(sketch, "E97.right", {"start": v(1543.05, 812.8) * mm, "end": v(1543.05, 76.2) * mm});
            skLineSegment(sketch, "E98.bottom", {"start": v(0, 889) * mm, "end": v(936.18, 889) * mm});
            skLineSegment(sketch, "E98.top", {"start": v(0, 850.9) * mm, "end": v(936.18, 850.9) * mm});
            skLineSegment(sketch, "E98.left", {"start": v(0, 889) * mm, "end": v(0, 850.9) * mm});
            skLineSegment(sketch, "E98.right", {"start": v(936.18, 889) * mm, "end": v(936.18, 850.9) * mm});
            skSolve(sketch);
        }
        {
            var Q0;
            Q0 = qSketchRegion(id + "F9", true);
            var Q1;
            Q1=makeQuery(id+"F9.imprint","IMPRINT",FACE,{"disambiguationData":[TD([[makeQuery(id+"F9.imprint","IMPRINT",EDGE,{"derivedFrom":sQuery(id+"F9.wireOp",EDGE,"E97.bottom")}),1.0]])]});
            var Q2;
            Q2=makeQuery(id+"F9.imprint","IMPRINT",FACE,{"disambiguationData":[TD([[makeQuery(id+"F9.imprint","IMPRINT",EDGE,{"derivedFrom":sQuery(id+"F9.wireOp",EDGE,"E93.bottom")}),1.0]])]});
            var Q3;
            Q3=makeQuery(id+"F9.imprint","IMPRINT",FACE,{"disambiguationData":[TD([[makeQuery(id+"F9.imprint","IMPRINT",EDGE,{"derivedFrom":sQuery(id+"F9.wireOp",EDGE,"E96.bottom")}),1.0]])]});
            var Q4;
            Q4=makeQuery(id+"F9.imprint","IMPRINT",FACE,{"disambiguationData":[TD([[makeQuery(id+"F9.imprint","IMPRINT",EDGE,{"derivedFrom":sQuery(id+"F9.wireOp",EDGE,"E94.bottom")}),1.0]])]});
            var Q5;
            Q5=makeQuery(id+"F9.imprint","IMPRINT",FACE,{"disambiguationData":[TD([[makeQuery(id+"F9.imprint","IMPRINT",EDGE,{"derivedFrom":sQuery(id+"F9.wireOp",EDGE,"E95.bottom")}),1.0]])]});
            extrude(context, id + "F10", {"entities" : qUnion([Q0, Q1, Q2, Q3, Q4, Q5]), "depth" : 88.9 * mm});
        }
        {
            var Q0;
            Q0=makeQuery(id+"F10.opExtrude","CAP_FACE",FACE,{"disambiguationData":[OSD([sQuery(id+"F9.wireOp",EDGE,"E86.bottom"),sQuery(id+"F9.wireOp",EDGE,"E86.top"),sQuery(id+"F9.wireOp",EDGE,"E87.bottom"),sQuery(id+"F9.wireOp",EDGE,"E87.top"),sQuery(id+"F9.wireOp",EDGE,"E87.left"),sQuery(id+"F9.wireOp",EDGE,"E87.right"),sQuery(id+"F9.wireOp",EDGE,"E88.bottom"),sQuery(id+"F9.wireOp",EDGE,"E88.top"),sQuery(id+"F9.wireOp",EDGE,"E88.left"),sQuery(id+"F9.wireOp",EDGE,"E88.right"),sQuery(id+"F9.wireOp",EDGE,"E91.MirrorCS"),sQuery(id+"F9.wireOp",EDGE,"E92.MirrorCS"),sQuery(id+"F9.wireOp",EDGE,"E93.left"),sQuery(id+"F9.wireOp",EDGE,"E93.right"),sQuery(id+"F9.wireOp",EDGE,"E94.left"),sQuery(id+"F9.wireOp",EDGE,"E94.right"),sQuery(id+"F9.wireOp",EDGE,"E95.left"),sQuery(id+"F9.wireOp",EDGE,"E95.right"),sQuery(id+"F9.wireOp",EDGE,"E96.left"),sQuery(id+"F9.wireOp",EDGE,"E96.right"),sQuery(id+"F9.wireOp",EDGE,"E97.left"),sQuery(id+"F9.wireOp",EDGE,"E97.right")])],"isStart":false});
            var sketch = newSketch(context, id + "F11", { "sketchPlane" : qUnion([Q0])});
            skLineSegment(sketch, "E99.bottom", {"start": v(3086.1, 889) * mm, "end": v(1257.3, 889) * mm});
            skLineSegment(sketch, "E99.top", {"start": v(1257.3, 850.9) * mm, "end": v(3086.1, 850.9) * mm});
            skLineSegment(sketch, "E99.left", {"start": v(1257.3, 889) * mm, "end": v(1257.3, 850.9) * mm});
            skLineSegment(sketch, "E99.right", {"start": v(3086.1, 889) * mm, "end": v(3086.1, 850.9) * mm});
            skLineSegment(sketch, "E100.MirrorCS", {"start": v(1257.3, 0) * mm, "end": v(1257.3, 38.1) * mm});
            skLineSegment(sketch, "E101.MirrorCS", {"start": v(3086.1, 0) * mm, "end": v(3086.1, 38.1) * mm});
            skLineSegment(sketch, "E102.MirrorCS", {"start": v(1257.3, 38.1) * mm, "end": v(3086.1, 38.1) * mm});
            skLineSegment(sketch, "E103.MirrorCS", {"start": v(3086.1, 0) * mm, "end": v(1257.3, 0) * mm});
            skLineSegment(sketch, "E104.bottom", {"start": v(1257.3, 889) * mm, "end": v(1219.2, 889) * mm});
            skLineSegment(sketch, "E104.top", {"start": v(1257.3, 0) * mm, "end": v(1219.2, 0) * mm});
            skLineSegment(sketch, "E104.left", {"start": v(1257.3, 889) * mm, "end": v(1257.3, 0) * mm});
            skLineSegment(sketch, "E104.right", {"start": v(1219.2, 889) * mm, "end": v(1219.2, 0) * mm});
            skLineSegment(sketch, "E105.bottom", {"start": v(3086.1, 889) * mm, "end": v(3124.2, 889) * mm});
            skLineSegment(sketch, "E105.top", {"start": v(3086.1, 0) * mm, "end": v(3124.2, 0) * mm});
            skLineSegment(sketch, "E105.left", {"start": v(3086.1, 889) * mm, "end": v(3086.1, 0) * mm});
            skLineSegment(sketch, "E105.right", {"start": v(3124.2, 889) * mm, "end": v(3124.2, 0) * mm});
            skSolve(sketch);
        }
        {
            var Q0;
            Q0 = qSketchRegion(id + "F11", true);
            extrude(context, id + "F12", {"entities" : qUnion([Q0]), "depth" : 25.4 * mm, "hasSecondDirection" : true, "secondDirectionOppositeDirection" : true, "secondDirectionDepth" : 114.3 * mm});
        }
        {
            var Q0;
            Q0=makeQuery(id+"F10.opExtrude","CAP_FACE",FACE,{"disambiguationData":[OSD([sQuery(id+"F9.wireOp",EDGE,"E86.bottom"),sQuery(id+"F9.wireOp",EDGE,"E86.top"),sQuery(id+"F9.wireOp",EDGE,"E87.bottom"),sQuery(id+"F9.wireOp",EDGE,"E87.top"),sQuery(id+"F9.wireOp",EDGE,"E87.left"),sQuery(id+"F9.wireOp",EDGE,"E87.right"),sQuery(id+"F9.wireOp",EDGE,"E88.bottom"),sQuery(id+"F9.wireOp",EDGE,"E88.top"),sQuery(id+"F9.wireOp",EDGE,"E88.left"),sQuery(id+"F9.wireOp",EDGE,"E88.right"),sQuery(id+"F9.wireOp",EDGE,"E91.MirrorCS"),sQuery(id+"F9.wireOp",EDGE,"E92.MirrorCS"),sQuery(id+"F9.wireOp",EDGE,"E93.left"),sQuery(id+"F9.wireOp",EDGE,"E93.right"),sQuery(id+"F9.wireOp",EDGE,"E94.left"),sQuery(id+"F9.wireOp",EDGE,"E94.right"),sQuery(id+"F9.wireOp",EDGE,"E95.left"),sQuery(id+"F9.wireOp",EDGE,"E95.right"),sQuery(id+"F9.wireOp",EDGE,"E96.left"),sQuery(id+"F9.wireOp",EDGE,"E96.right"),sQuery(id+"F9.wireOp",EDGE,"E97.left"),sQuery(id+"F9.wireOp",EDGE,"E97.right")])],"isStart":false});
            var sketch = newSketch(context, id + "F13", { "sketchPlane" : qUnion([Q0])});
            skLineSegment(sketch, "E106.bottom", {"start": v(1257.3, 850.9) * mm, "end": v(3086.1, 850.9) * mm});
            skLineSegment(sketch, "E106.top", {"start": v(1257.3, 38.1) * mm, "end": v(3086.1, 38.1) * mm});
            skLineSegment(sketch, "E106.left", {"start": v(1257.3, 850.9) * mm, "end": v(1257.3, 38.1) * mm});
            skLineSegment(sketch, "E106.right", {"start": v(3086.1, 850.9) * mm, "end": v(3086.1, 38.1) * mm});
            skSolve(sketch);
        }
        {
            var Q0;
            Q0 = qSketchRegion(id + "F13", true);
            extrude(context, id + "F14", {"entities" : qUnion([Q0]), "operationType" : NewBodyOperationType.ADD, "depth" : 19.05 * mm});
        }
        {
            var Q0;
            Q0=makeQuery(id+"F14.opExtrude","CAP_FACE",FACE,{"disambiguationData":[OSD([sQuery(id+"F13.wireOp",EDGE,"E106.bottom"),sQuery(id+"F13.wireOp",EDGE,"E106.top"),sQuery(id+"F13.wireOp",EDGE,"E106.left"),sQuery(id+"F13.wireOp",EDGE,"E106.right")])],"isStart":false});
            var sketch = newSketch(context, id + "F15", { "sketchPlane" : qUnion([Q0])});
            skLineSegment(sketch, "E107.bottom", {"start": v(1257.3, 850.9) * mm, "end": v(3086.1, 850.9) * mm});
            skLineSegment(sketch, "E107.top", {"start": v(1257.3, 38.1) * mm, "end": v(3086.1, 38.1) * mm});
            skLineSegment(sketch, "E107.left", {"start": v(1257.3, 850.9) * mm, "end": v(1257.3, 38.1) * mm});
            skLineSegment(sketch, "E107.right", {"start": v(3086.1, 850.9) * mm, "end": v(3086.1, 38.1) * mm});
            skSolve(sketch);
        }
        {
            var Q0;
            Q0 = qSketchRegion(id + "F15", true);
            extrude(context, id + "F16", {"entities" : qUnion([Q0]), "operationType" : NewBodyOperationType.ADD, "depth" : 6.35 * mm});
        }
    });
